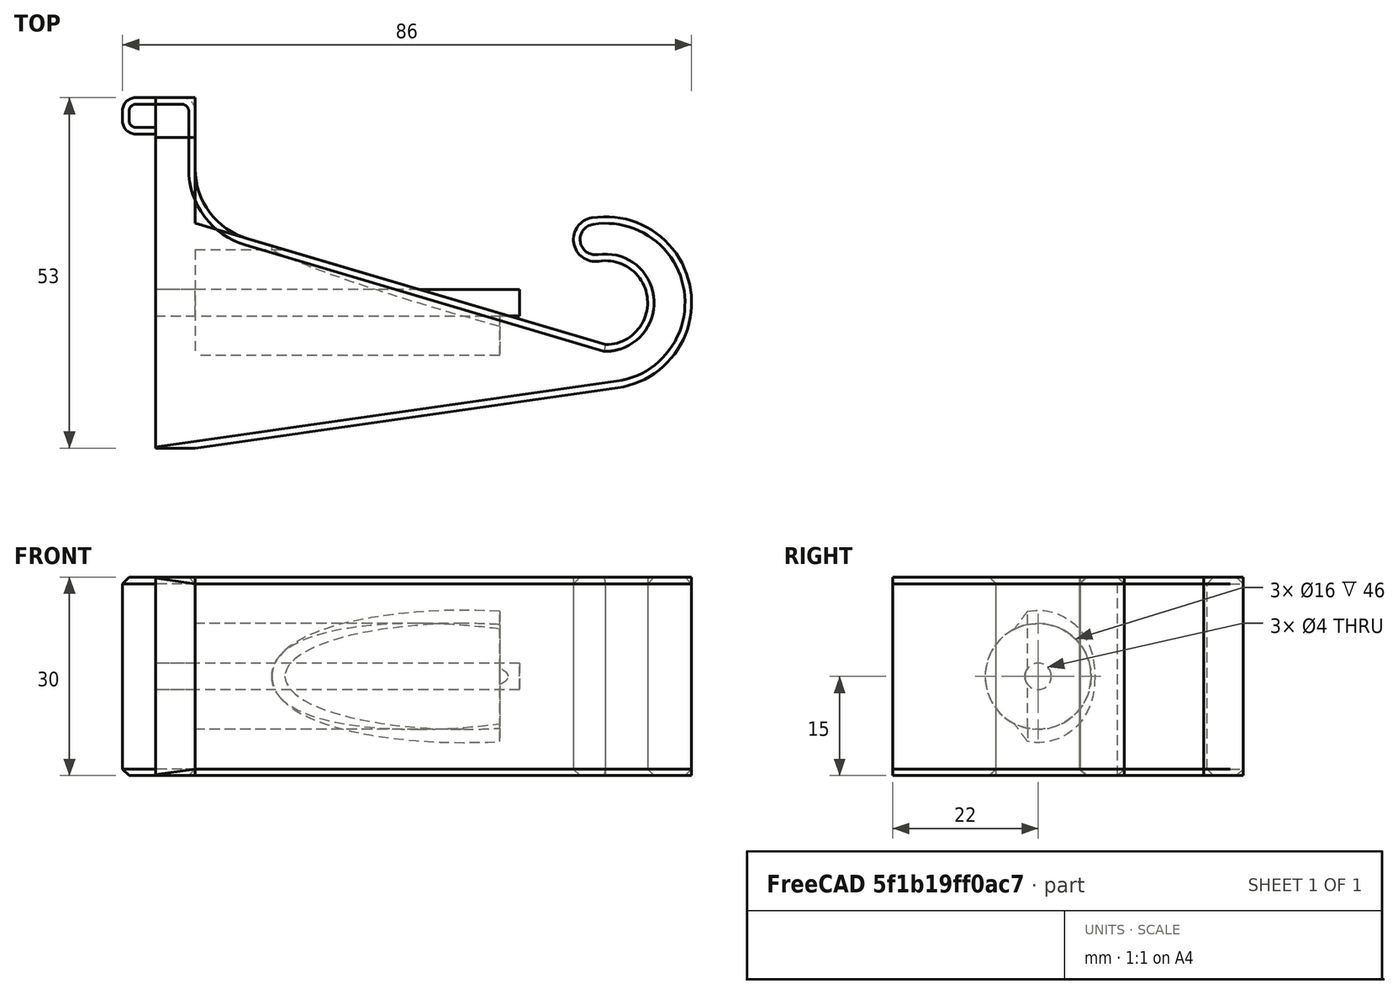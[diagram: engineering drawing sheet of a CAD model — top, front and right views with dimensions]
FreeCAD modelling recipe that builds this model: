
FCSTD DOCUMENT  (FreeCAD 0.16R)
Label: BabyGateLong-hook
License: All rights reserved
LicenseURL: http://en.wikipedia.org/wiki/All_rights_reserved
objects: Sketcher::SketchObject×5, PartDesign::Chamfer×4, PartDesign::Pad×3, PartDesign::Pocket×2, PartDesign::Fillet×2, Mesh::Feature×1
note: 21 computed .brp shape members not serialized (recipe doc carries the construction recipe); baked Part::Feature solids carry a one-line shape summary decoded from their .brp

FEATURE [Sketcher::SketchObject] Sketch001
  sketch-geometry (9):
    g0: ArcOfCircle CenterX=0 CenterY=0 CenterZ=0 NormalX=0 NormalY=0 NormalZ=1 Radius=6.35 StartAngle=4.71239 EndAngle=8.01212
    g1: ArcOfCircle CenterX=0 CenterY=0 CenterZ=0 NormalX=0 NormalY=0 NormalZ=1 Radius=13 StartAngle=4.85445 EndAngle=8.01212
    g2: LineSegment StartX=1.84063 StartY=-12.869 StartZ=0 EndX=-62 EndY=-22 EndZ=0
    g3: LineSegment StartX=2e-12 StartY=-6.35 StartZ=0 EndX=-62 EndY=12 EndZ=0
    g4: LineSegment StartX=-62 StartY=12 StartZ=0 EndX=-62 EndY=25 EndZ=0
    g5: LineSegment StartX=-62 StartY=25 StartZ=0 EndX=-68 EndY=25 EndZ=0
    g6: LineSegment StartX=-68 StartY=25 StartZ=0 EndX=-68 EndY=-22 EndZ=0
    g7: LineSegment StartX=-68 StartY=-22 StartZ=0 EndX=-62 EndY=-22 EndZ=0
    g8: ArcOfCircle CenterX=-1.52364 CenterY=9.55427 CenterZ=0 NormalX=0 NormalY=0 NormalZ=1 Radius=3.325 StartAngle=1.72894 EndAngle=4.87053
  constraints (28):
    c: Coincident(g0,g-1)
    c: PointOnObject(g0,g-2)
    c: Radius(g0) = 6.35
    c: DistanceX(g0,g-1) = 1
    c: Radius(g1) = 13
    c: Coincident(g1,g-1)
    c: Coincident(g2,g1)
    c: DistanceX(g3) = -62
    c: DistanceX(g2) = -62
    c: Coincident(g4,g3)
    c: Vertical(g4)
    c: Coincident(g4,g5)
    c: Coincident(g5,g6)
    c: Vertical(g6)
    c: Coincident(g6,g7)
    c: Horizontal(g5)
    c: Horizontal(g7)
    c: DistanceX(g5,g5) = 6
    c: Tangent(g8,g1)
    c: Coincident(g8,g1)
    c: Coincident(g0,g8)
    c: Coincident(g2,g7)
    c: Tangent(g2,g1)
    c: DistanceY(g5) = 25
    c: DistanceY(g6) = -22
    c: Coincident(g3,g0)
    c: Tangent(g0,g8)
    c: DistanceY(g3) = 12
FEATURE [PartDesign::Pad] Pad
  Length = 30
  Length2 = 100
  Sketch = -> Sketch001
  Type = 0
FEATURE [Sketcher::SketchObject] Sketch002
  Placement = pos=(-68,0,0) rot=(0.57735,-0.57735,-0.57735;2.0944rad)
  Support = -> Pad [Face7]
  sketch-geometry (1):
    g0: Circle CenterX=0 CenterY=15 CenterZ=0 NormalX=0 NormalY=0 NormalZ=1 Radius=2
  constraints (3):
    c: PointOnObject(g0,g-2)
    c: DistanceY(g-1,g0) = 15
    c: Radius(g0) = 2
FEATURE [PartDesign::Pocket] Pocket
  Length = 55
  Sketch = -> Sketch002
  Type = 0
FEATURE [Sketcher::SketchObject] Sketch003
  Placement = pos=(-62,0,0) rot=(0.57735,0.57735,0.57735;2.0944rad)
  Support = -> Pocket [Face5]
  sketch-geometry (1):
    g0: Circle CenterX=0 CenterY=15 CenterZ=0 NormalX=0 NormalY=0 NormalZ=1 Radius=8
  constraints (3):
    c: PointOnObject(g0,g-2)
    c: DistanceY(g0) = 15
    c: Radius(g0) = 8
FEATURE [PartDesign::Pocket] Pocket001
  Length = 46
  Reversed = true
  Sketch = -> Sketch003
  Type = 0
FEATURE [PartDesign::Fillet] Fillet
  Base = -> Pocket001 [Edge4]
  Radius = 11
FEATURE [Sketcher::SketchObject] Sketch
  ExternalGeometry = -> [Fillet]
  Placement = pos=(0,25,0) rot=(0,0.707107,0.707107;3.14159rad)
  Support = -> Fillet [Face12]
  sketch-geometry (4):
    g0: LineSegment StartX=62 StartY=30 StartZ=0 EndX=68 EndY=30 EndZ=0
    g1: LineSegment StartX=68 StartY=30 StartZ=0 EndX=68 EndY=0 EndZ=0
    g2: LineSegment StartX=68 StartY=0 StartZ=0 EndX=62 EndY=0 EndZ=0
    g3: LineSegment StartX=62 StartY=0 StartZ=0 EndX=62 EndY=30 EndZ=0
  constraints (8):
    c: Coincident(g-5,g0)
    c: Coincident(g0,g-5)
    c: Coincident(g0,g1)
    c: Coincident(g1,g-6)
    c: Coincident(g1,g2)
    c: Coincident(g2,g-6)
    c: Coincident(g2,g3)
    c: Coincident(g3,g0)
FEATURE [PartDesign::Pad] Pad001
  Length = 6
  Length2 = 100
  Sketch = -> Sketch
  Type = 0
FEATURE [Sketcher::SketchObject] Sketch004
  ExternalGeometry = -> [Pad001]
  Placement = pos=(-68,0,0) rot=(0.57735,-0.57735,-0.57735;2.0944rad)
  Support = -> Pad001 [Face3]
  sketch-geometry (4):
    g0: LineSegment StartX=-31 StartY=30 StartZ=0 EndX=-31 EndY=0 EndZ=0
    g1: LineSegment StartX=-31 StartY=0 StartZ=0 EndX=-25.5 EndY=0 EndZ=0
    g2: LineSegment StartX=-25.5 StartY=0 StartZ=0 EndX=-25.5 EndY=30 EndZ=0
    g3: LineSegment StartX=-25.5 StartY=30 StartZ=0 EndX=-31 EndY=30 EndZ=0
  constraints (10):
    c: Coincident(g-4,g0)
    c: Coincident(g0,g-5)
    c: Coincident(g0,g1)
    c: Coincident(g1,g2)
    c: Vertical(g2)
    c: Coincident(g2,g3)
    c: Coincident(g3,g0)
    c: Horizontal(g3)
    c: Horizontal(g1)
    c: DistanceX(g1) = -25.5
FEATURE [PartDesign::Pad] Pad002
  Length = 5
  Length2 = 100
  Sketch = -> Sketch004
  Type = 0
FEATURE [PartDesign::Fillet] Fillet001
  Base = -> Pad002 [Edge3,Edge40,Edge45]
  Radius = 2
FEATURE [PartDesign::Chamfer] Chamfer
  Base = -> Fillet001 [Edge23,Edge40]
  Size = 1
FEATURE [PartDesign::Chamfer] Chamfer001
  Base = -> Chamfer [Edge39]
  Size = 1
FEATURE [PartDesign::Chamfer] Chamfer002
  Base = -> Chamfer001 [Edge17]
  Size = 1
FEATURE [PartDesign::Chamfer] Chamfer003
  Base = -> Chamfer002 [Edge22]
  Size = 2
FEATURE [Mesh::Feature] Mesh  label="Chamfer003 (Meshed)"
